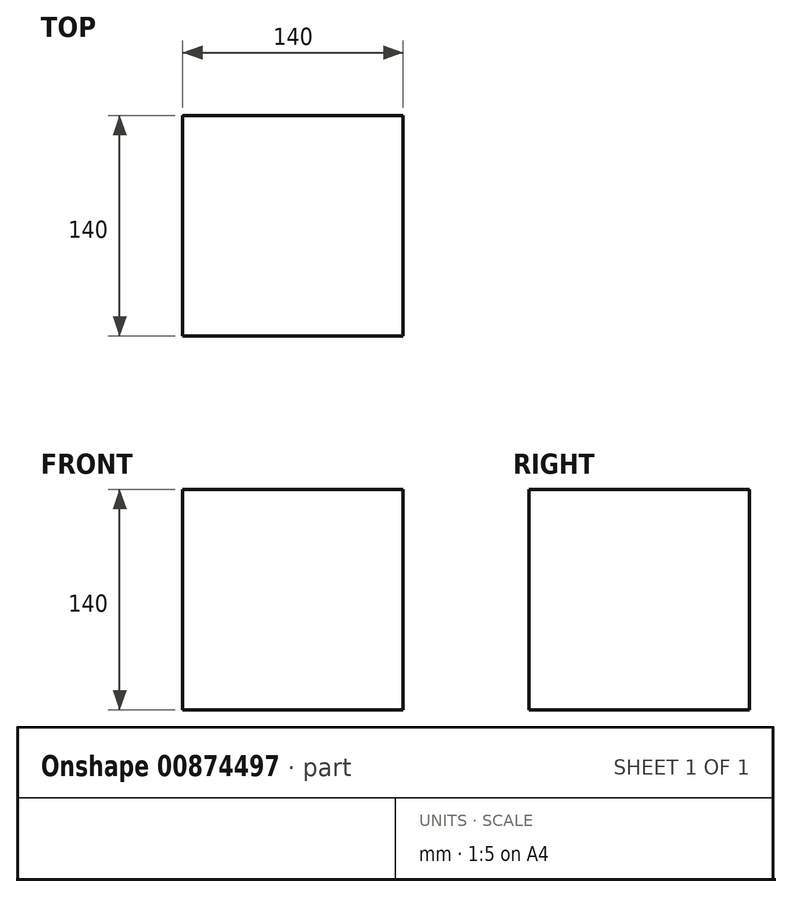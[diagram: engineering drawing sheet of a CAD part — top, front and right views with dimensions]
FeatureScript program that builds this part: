
annotation { "Feature Type Name" : "Feature", "Feature Type Description" : "" }
export const myFeature = defineFeature(function(context is Context, id is Id, definition is map)
    precondition{}
    {
        {
            var Q0;
            Q0=qCreatedBy(makeId("Top.planeOp"),FACE);
            var sketch = newSketch(context, id + "F0", { "sketchPlane" : qUnion([Q0])});
            skLineSegment(sketch, "E0.bottom", {"start": v(70, -70) * mm, "end": v(-70, -70) * mm});
            skLineSegment(sketch, "E0.top", {"start": v(70, 70) * mm, "end": v(-70, 70) * mm});
            skLineSegment(sketch, "E0.left", {"start": v(70, -70) * mm, "end": v(70, 70) * mm});
            skLineSegment(sketch, "E0.right", {"start": v(-70, -70) * mm, "end": v(-70, 70) * mm});
            skPoint(sketch, "E0.middle", {"position": v(0, 0) * mm});
            skSolve(sketch);
        }
        {
            var Q0;
            Q0 = qSketchRegion(id + "F0", true);
            extrude(context, id + "F1", {"entities" : qUnion([Q0]), "depth" : 140 * mm, "offsetDistance" : 25 * mm});
        }
    });
